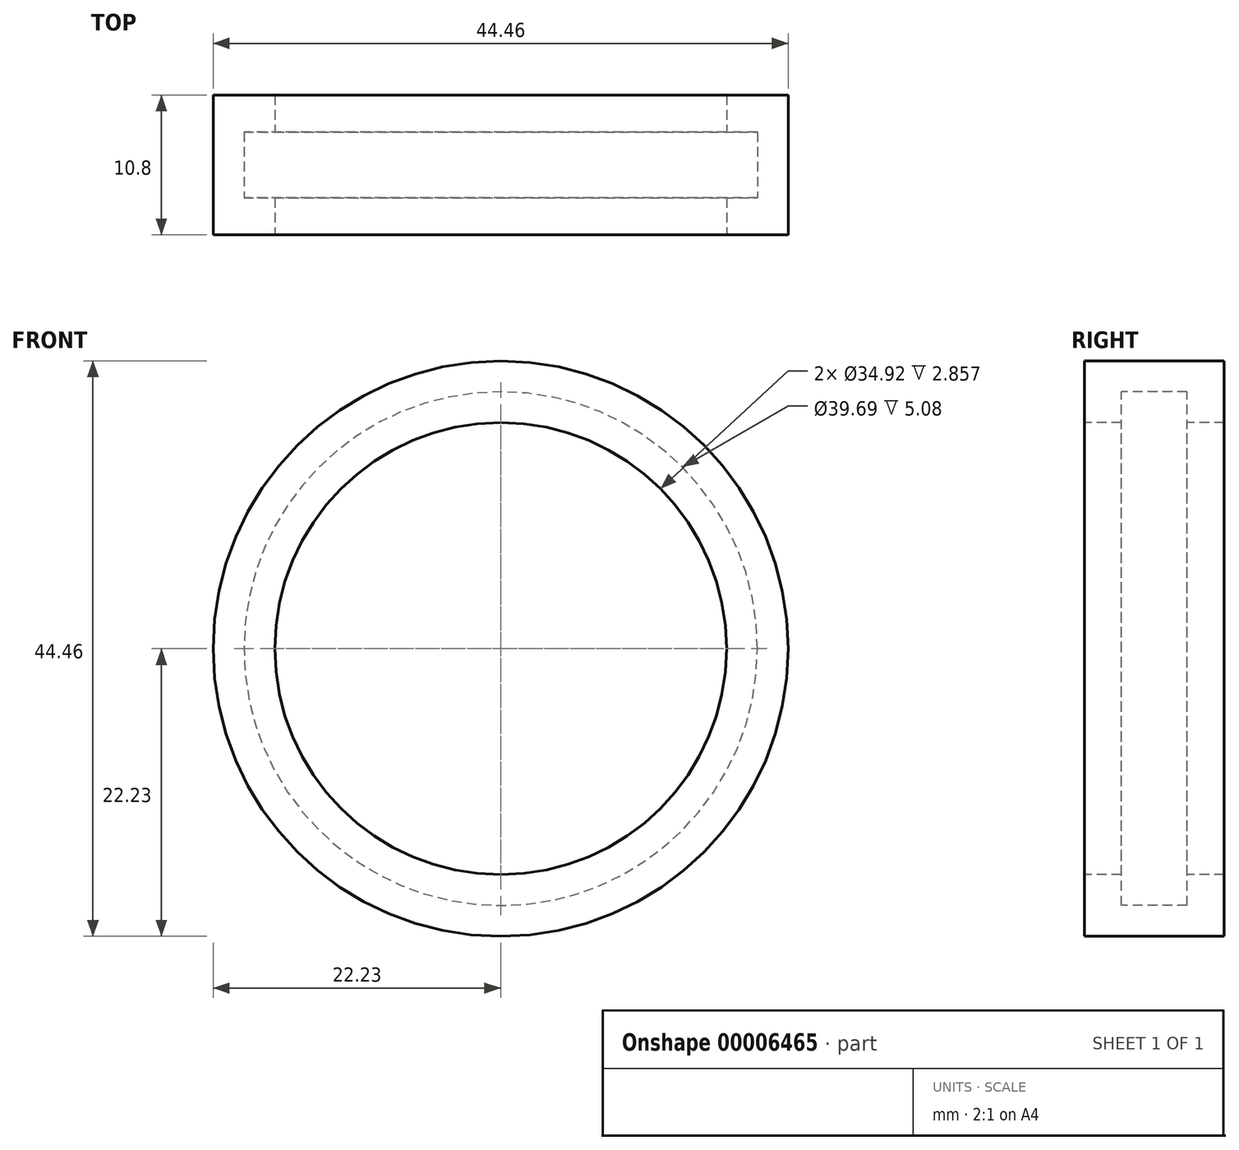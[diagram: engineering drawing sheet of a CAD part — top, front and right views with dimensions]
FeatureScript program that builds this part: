
annotation { "Feature Type Name" : "Feature", "Feature Type Description" : "" }
export const myFeature = defineFeature(function(context is Context, id is Id, definition is map)
    precondition{}
    {
        {
            var Q0;
            Q0=qCreatedBy(makeId("Right.planeOp"),FACE);
            var sketch = newSketch(context, id + "F0", { "sketchPlane" : qUnion([Q0])});
            skLineSegment(sketch, "E0", {"start": v(0, 17.46) * mm, "end": v(0, 22.23) * mm});
            skLineSegment(sketch, "E1", {"start": v(0, 22.23) * mm, "end": v(10.8, 22.23) * mm});
            skLineSegment(sketch, "E2", {"start": v(10.8, 22.23) * mm, "end": v(10.8, 17.46) * mm});
            skLineSegment(sketch, "E3", {"start": v(10.8, 17.46) * mm, "end": v(7.94, 17.46) * mm});
            skLineSegment(sketch, "E4", {"start": v(7.94, 17.46) * mm, "end": v(7.94, 19.84) * mm});
            skLineSegment(sketch, "E5", {"start": v(7.94, 19.84) * mm, "end": v(2.86, 19.84) * mm});
            skLineSegment(sketch, "E6", {"start": v(2.86, 19.84) * mm, "end": v(2.86, 17.46) * mm});
            skLineSegment(sketch, "E7", {"start": v(2.86, 17.46) * mm, "end": v(0, 17.46) * mm});
            skLineSegment(sketch, "E8", {"start": v(0, 0) * mm, "end": v(15.75, 0) * mm, "construction": true});
            skSolve(sketch);
        }
        {
            var Q0;
            Q0=makeQuery(id+"F0.imprint","IMPRINT",FACE,{"disambiguationData":[TD([[makeQuery(id+"F0.imprint","IMPRINT",EDGE,{"derivedFrom":sQuery(id+"F0.wireOp",EDGE,"E0")}),-1.0]])]});
            var Q1;
            Q1=sQuery(id+"F0.wireOp",EDGE,"E8");
            revolve(context, id + "F1", {"entities" : qUnion([Q0]), "axis" : qUnion([Q1]), "revolveType" : RevolveType.FULL});
        }
    });
